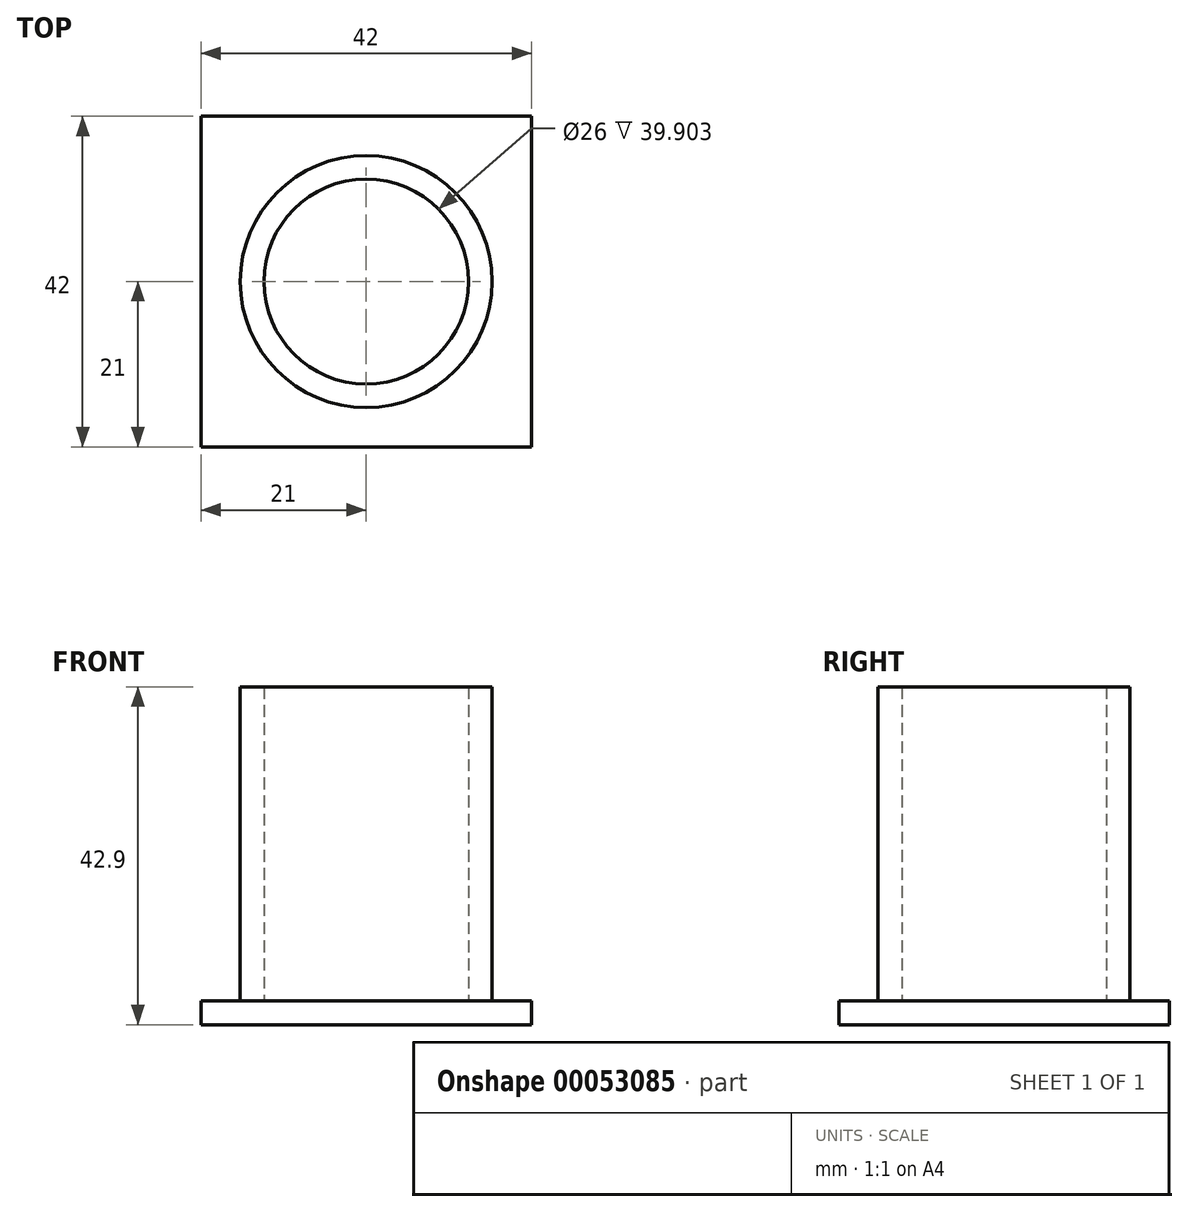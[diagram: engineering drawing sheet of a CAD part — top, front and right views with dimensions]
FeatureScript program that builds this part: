
annotation { "Feature Type Name" : "Feature", "Feature Type Description" : "" }
export const myFeature = defineFeature(function(context is Context, id is Id, definition is map)
    precondition{}
    {
        {
            var Q0;
            Q0=qCreatedBy(makeId("Top.planeOp"),FACE);
            var sketch = newSketch(context, id + "F0", { "sketchPlane" : qUnion([Q0])});
            skCircle(sketch, "E0", {"center": v(0, 0) * mm, "radius": 13 * mm});
            skCircle(sketch, "E1", {"center": v(0, 0) * mm, "radius": 16 * mm});
            skSolve(sketch);
        }
        {
            var Q0;
            Q0=makeQuery(id+"F0.imprint","IMPRINT",FACE,{"disambiguationData":[TD([[makeQuery(id+"F0.imprint","IMPRINT",EDGE,{"derivedFrom":sQuery(id+"F0.wireOp",EDGE,"E0")}),-1.0]])]});
            extrude(context, id + "F1", {"entities" : qUnion([Q0]), "depth" : 39.9 * mm});
        }
        {
            var Q0;
            Q0=makeQuery(id+"F1.opExtrude","CAP_FACE",FACE,{"disambiguationData":[OSD([sQuery(id+"F0.wireOp",EDGE,"E0"),sQuery(id+"F0.wireOp",EDGE,"E1")])],"isStart":true});
            var sketch = newSketch(context, id + "F2", { "sketchPlane" : qUnion([Q0])});
            skLineSegment(sketch, "E2.bottom", {"start": v(-21, 21) * mm, "end": v(21, 21) * mm});
            skLineSegment(sketch, "E2.top", {"start": v(-21, -21) * mm, "end": v(21, -21) * mm});
            skLineSegment(sketch, "E2.left", {"start": v(-21, 21) * mm, "end": v(-21, -21) * mm});
            skLineSegment(sketch, "E2.right", {"start": v(21, 21) * mm, "end": v(21, -21) * mm});
            skSolve(sketch);
        }
        {
            var Q0;
            Q0=makeQuery(id+"F2.imprint","IMPRINT",FACE,{"disambiguationData":[TD([[makeQuery(id+"F2.imprint","IMPRINT",EDGE,{"derivedFrom":sQuery(id+"F2.wireOp",EDGE,"E2.bottom")}),-1.0]])]});
            var Q1;
            Q1=makeQuery(id+"F2.imprint","IMPRINT",FACE,{"disambiguationData":[TD([[makeQuery(id+"F2.imprint","IMPRINT",EDGE,{"derivedFrom":makeQuery(id+"F1.opExtrude","CAP_EDGE",EDGE,{"disambiguationData":[OSD([sQuery(id+"F0.wireOp",EDGE,"E0")])],"isStart":true})}),-1.0]])]});
            var Q2;
            Q2=makeQuery(id+"F2.imprint","IMPRINT",FACE,{"disambiguationData":[TD([[makeQuery(id+"F2.imprint","IMPRINT",EDGE,{"derivedFrom":makeQuery(id+"F1.opExtrude","CAP_EDGE",EDGE,{"disambiguationData":[OSD([sQuery(id+"F0.wireOp",EDGE,"E0")])],"isStart":true})}),1.0]])]});
            extrude(context, id + "F3", {"entities" : qUnion([Q0, Q1, Q2]), "depth" : 3 * mm});
        }
    });
